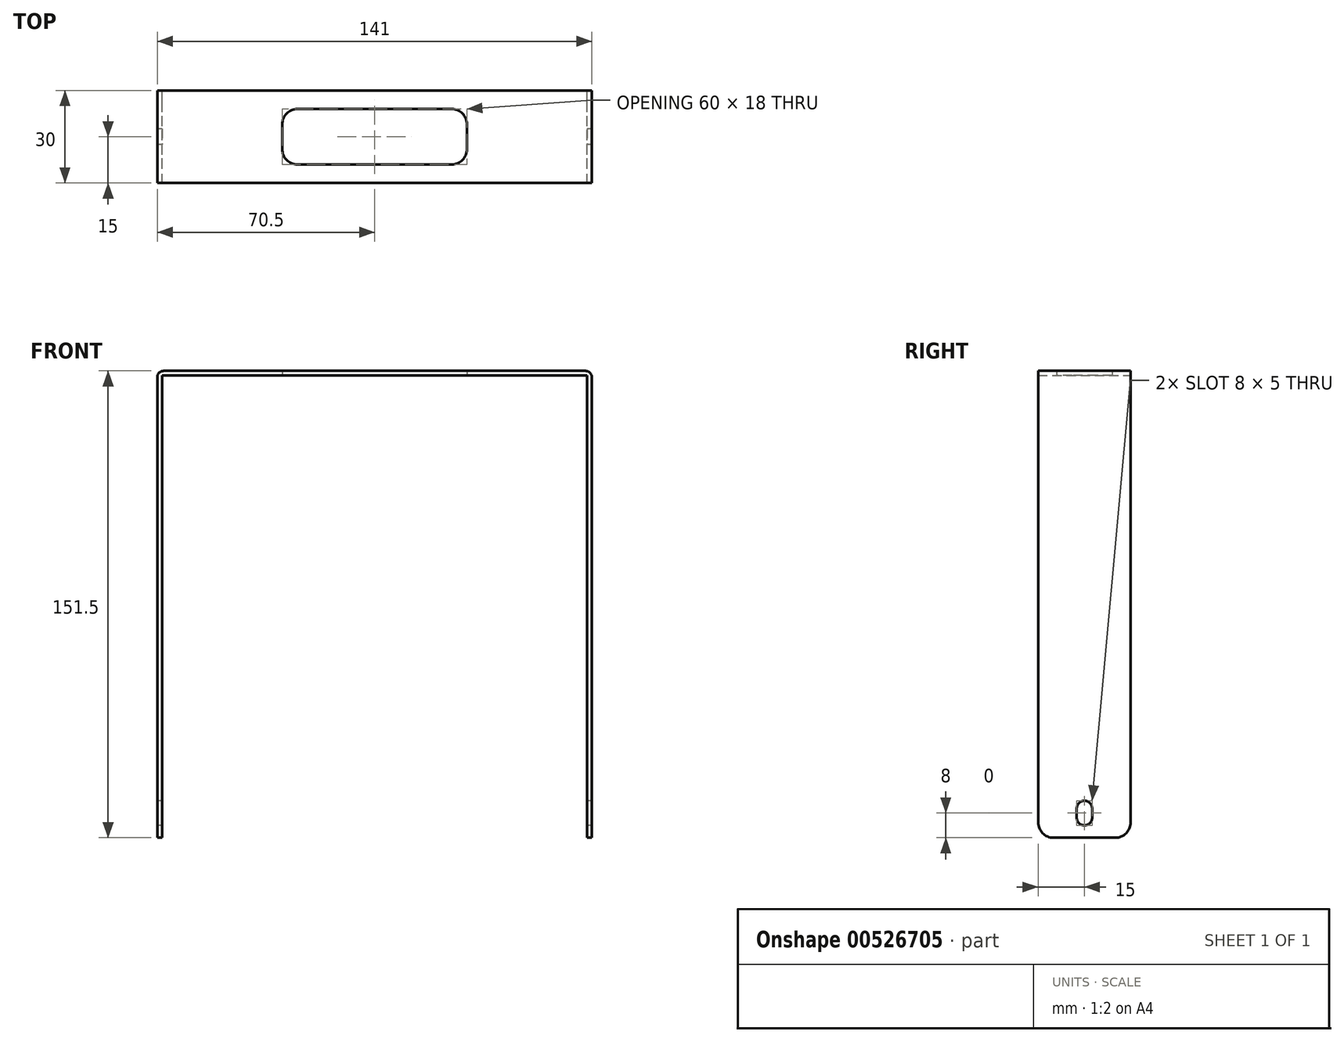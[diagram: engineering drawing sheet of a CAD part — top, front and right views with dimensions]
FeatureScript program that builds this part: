
annotation { "Feature Type Name" : "Feature", "Feature Type Description" : "" }
export const myFeature = defineFeature(function(context is Context, id is Id, definition is map)
    precondition{}
    {
        {
            var Q0;
            Q0=qCreatedBy(makeId("Top.planeOp"),FACE);
            var sketch = newSketch(context, id + "F0", { "sketchPlane" : qUnion([Q0])});
            skLineSegment(sketch, "E0.bottom", {"start": v(-70.5, 15) * mm, "end": v(70.5, 15) * mm});
            skLineSegment(sketch, "E0.top", {"start": v(-70.5, -15) * mm, "end": v(70.5, -15) * mm});
            skLineSegment(sketch, "E0.left", {"start": v(-70.5, 15) * mm, "end": v(-70.5, -15) * mm});
            skLineSegment(sketch, "E0.right", {"start": v(70.5, 15) * mm, "end": v(70.5, -15) * mm});
            skPoint(sketch, "E0.middle", {"position": v(0, 0) * mm});
            skLineSegment(sketch, "E1.bottom", {"start": v(-30, 9) * mm, "end": v(30, 9) * mm});
            skLineSegment(sketch, "E1.top", {"start": v(-30, -9) * mm, "end": v(30, -9) * mm});
            skLineSegment(sketch, "E1.left", {"start": v(-30, 9) * mm, "end": v(-30, -9) * mm});
            skLineSegment(sketch, "E1.right", {"start": v(30, 9) * mm, "end": v(30, -9) * mm});
            skSolve(sketch);
        }
        {
            var Q0;
            Q0=makeQuery(id+"F0.imprint","IMPRINT",FACE,{"disambiguationData":[TD([[makeQuery(id+"F0.imprint","IMPRINT",EDGE,{"derivedFrom":sQuery(id+"F0.wireOp",EDGE,"E0.bottom")}),-1.0]])]});
            extrude(context, id + "F1", {"entities" : qUnion([Q0]), "depth" : 1.5 * mm});
        }
        {
            var Q0;
            Q0=makeQuery(id+"F1.opExtrude","CAP_FACE",FACE,{"disambiguationData":[OSD([sQuery(id+"F0.wireOp",EDGE,"E0.bottom"),sQuery(id+"F0.wireOp",EDGE,"E0.top"),sQuery(id+"F0.wireOp",EDGE,"E0.left"),sQuery(id+"F0.wireOp",EDGE,"E0.right"),sQuery(id+"F0.wireOp",EDGE,"E1.bottom"),sQuery(id+"F0.wireOp",EDGE,"E1.top"),sQuery(id+"F0.wireOp",EDGE,"E1.left"),sQuery(id+"F0.wireOp",EDGE,"E1.right")])],"isStart":true});
            var sketch = newSketch(context, id + "F2", { "sketchPlane" : qUnion([Q0])});
            skLineSegment(sketch, "E2.bottom", {"start": v(-70.5, 15) * mm, "end": v(-69, 15) * mm});
            skLineSegment(sketch, "E2.top", {"start": v(-70.5, -15) * mm, "end": v(-69, -15) * mm});
            skLineSegment(sketch, "E2.left", {"start": v(-70.5, 15) * mm, "end": v(-70.5, -15) * mm});
            skLineSegment(sketch, "E2.right", {"start": v(-69, 15) * mm, "end": v(-69, -15) * mm});
            skLineSegment(sketch, "E3.bottom", {"start": v(70.5, 15) * mm, "end": v(69, 15) * mm});
            skLineSegment(sketch, "E3.top", {"start": v(70.5, -15) * mm, "end": v(69, -15) * mm});
            skLineSegment(sketch, "E3.left", {"start": v(70.5, 15) * mm, "end": v(70.5, -15) * mm});
            skLineSegment(sketch, "E3.right", {"start": v(69, 15) * mm, "end": v(69, -15) * mm});
            skSolve(sketch);
        }
        {
            var Q0;
            Q0=makeQuery(id+"F2.imprint","IMPRINT",FACE,{"disambiguationData":[TD([[makeQuery(id+"F2.imprint","IMPRINT",EDGE,{"derivedFrom":sQuery(id+"F2.wireOp",EDGE,"E2.bottom")}),-1.0]])]});
            var Q1;
            Q1=makeQuery(id+"F2.imprint","IMPRINT",FACE,{"disambiguationData":[TD([[makeQuery(id+"F2.imprint","IMPRINT",EDGE,{"derivedFrom":sQuery(id+"F2.wireOp",EDGE,"E3.bottom")}),-1.0]])]});
            extrude(context, id + "F3", {"entities" : qUnion([Q0, Q1]), "operationType" : NewBodyOperationType.ADD, "depth" : 150 * mm, "offsetDistance" : 25 * mm});
        }
        {
            var Q0;
            Q0=makeQuery(id+"F0S0k0WWYooROMG_1.opExtrude","SWEPT_EDGE",EDGE,{"disambiguationData":[OSD([sQuery(id+"FLBt2EZMuTxA5II_1.wireOp",EDGE,"gpiNC70y-X5YM-kdtF-PmHe-AwHMzD0TUCJG.top"),sQuery(id+"FLBt2EZMuTxA5II_1.wireOp",EDGE,"gpiNC70y-X5YM-kdtF-PmHe-AwHMzD0TUCJG.right")])]});
            var Q1;
            Q1=makeQuery(id+"F0S0k0WWYooROMG_1.opExtrude","SWEPT_EDGE",EDGE,{"disambiguationData":[OSD([sQuery(id+"FLBt2EZMuTxA5II_1.wireOp",EDGE,"gpiNC70y-X5YM-kdtF-PmHe-AwHMzD0TUCJG.bottom"),sQuery(id+"FLBt2EZMuTxA5II_1.wireOp",EDGE,"gpiNC70y-X5YM-kdtF-PmHe-AwHMzD0TUCJG.right")])]});
            var Q2;
            Q2=makeQuery(id+"FBcZxHqoujWJ6ID_1.1.F0S0k0WWYooROMG_1.opExtrude","SWEPT_EDGE",EDGE,{"disambiguationData":[OSD([sQuery(id+"FLBt2EZMuTxA5II_1.wireOp",EDGE,"gpiNC70y-X5YM-kdtF-PmHe-AwHMzD0TUCJG.top"),sQuery(id+"FLBt2EZMuTxA5II_1.wireOp",EDGE,"gpiNC70y-X5YM-kdtF-PmHe-AwHMzD0TUCJG.right")])]});
            var Q3;
            Q3=makeQuery(id+"FBcZxHqoujWJ6ID_1.1.F0S0k0WWYooROMG_1.opExtrude","SWEPT_EDGE",EDGE,{"disambiguationData":[OSD([sQuery(id+"FLBt2EZMuTxA5II_1.wireOp",EDGE,"gpiNC70y-X5YM-kdtF-PmHe-AwHMzD0TUCJG.bottom"),sQuery(id+"FLBt2EZMuTxA5II_1.wireOp",EDGE,"gpiNC70y-X5YM-kdtF-PmHe-AwHMzD0TUCJG.right")])]});
            var Q4;
            Q4=makeQuery(id+"F1.opExtrude","SWEPT_EDGE",EDGE,{"disambiguationData":[OSD([sQuery(id+"F0.wireOp",EDGE,"E1.bottom"),sQuery(id+"F0.wireOp",EDGE,"E1.right")])]});
            var Q5;
            Q5=makeQuery(id+"F1.opExtrude","SWEPT_EDGE",EDGE,{"disambiguationData":[OSD([sQuery(id+"F0.wireOp",EDGE,"E1.top"),sQuery(id+"F0.wireOp",EDGE,"E1.right")])]});
            var Q6;
            Q6=makeQuery(id+"F1.opExtrude","SWEPT_EDGE",EDGE,{"disambiguationData":[OSD([sQuery(id+"F0.wireOp",EDGE,"E1.top"),sQuery(id+"F0.wireOp",EDGE,"E1.left")])]});
            var Q7;
            Q7=makeQuery(id+"F1.opExtrude","SWEPT_EDGE",EDGE,{"disambiguationData":[OSD([sQuery(id+"F0.wireOp",EDGE,"E1.bottom"),sQuery(id+"F0.wireOp",EDGE,"E1.left")])]});
            fillet(context, id + "F4", {"entities" : qUnion([Q0, Q1, Q2, Q3, Q4, Q5, Q6, Q7]), "radius" : 5 * mm, "tangentPropagation" : true, "allowEdgeOverflow" : false});
        }
        {
            var Q0;
            Q0=makeQuery(id+"F3.opExtrude","CAP_EDGE",EDGE,{"disambiguationData":[OSD([sQuery(id+"F2.wireOp",EDGE,"E2.bottom")])],"isStart":false});
            var Q1;
            Q1=makeQuery(id+"F3.opExtrude","CAP_EDGE",EDGE,{"disambiguationData":[OSD([sQuery(id+"F2.wireOp",EDGE,"E2.top")])],"isStart":false});
            var Q2;
            Q2=makeQuery(id+"F3.opExtrude","CAP_EDGE",EDGE,{"disambiguationData":[OSD([sQuery(id+"F2.wireOp",EDGE,"E3.bottom")])],"isStart":false});
            var Q3;
            Q3=makeQuery(id+"F3.opExtrude","CAP_EDGE",EDGE,{"disambiguationData":[OSD([sQuery(id+"F2.wireOp",EDGE,"E3.top")])],"isStart":false});
            fillet(context, id + "F5", {"entities" : qUnion([Q0, Q1, Q2, Q3]), "radius" : 5 * mm, "tangentPropagation" : true, "allowEdgeOverflow" : false});
        }
        {
            var Q0;
            Q0=makeQuery(id+"F3.boolean.opBoolean","MERGE",FACE,{"derivedFrom":[makeQuery(id+"F1.opExtrude","SWEPT_FACE",FACE,{"disambiguationData":[OSD([sQuery(id+"F0.wireOp",EDGE,"E0.left")])]}),makeQuery(id+"F3.opExtrude","SWEPT_FACE",FACE,{"disambiguationData":[OSD([sQuery(id+"F2.wireOp",EDGE,"E2.left")])]})]});
            var sketch = newSketch(context, id + "F6", { "sketchPlane" : qUnion([Q0])});
            skLineSegment(sketch, "E4", {"start": v(0, -150) * mm, "end": v(0, 1.5) * mm, "construction": true});
            skLineSegment(sketch, "E5.bottom", {"start": v(0, -146) * mm, "end": v(0, -146) * mm});
            skLineSegment(sketch, "E5.top", {"start": v(0, -138) * mm, "end": v(0, -138) * mm});
            skLineSegment(sketch, "E5.left", {"start": v(-2.5, -143.5) * mm, "end": v(-2.5, -140.5) * mm});
            skLineSegment(sketch, "E5.right", {"start": v(2.5, -143.5) * mm, "end": v(2.5, -140.5) * mm});
            skPoint(sketch, "E5.middle", {"position": v(0, -142) * mm});
            skPoint(sketch, "E6.visualSharp", {"position": v(-2.5, -138) * mm});
            skArc(sketch, "E6.filletArc", {"start": v(0, -138) * mm, "mid": v(-1.77, -138.73) * mm, "end": v(-2.5, -140.5) * mm});
            skPoint(sketch, "E7.visualSharp", {"position": v(2.5, -138) * mm});
            skArc(sketch, "E7.filletArc", {"start": v(2.5, -140.5) * mm, "mid": v(1.77, -138.73) * mm, "end": v(0, -138) * mm});
            skPoint(sketch, "E8.visualSharp", {"position": v(-2.5, -146) * mm});
            skArc(sketch, "E8.filletArc", {"start": v(-2.5, -143.5) * mm, "mid": v(-1.77, -145.27) * mm, "end": v(0, -146) * mm});
            skPoint(sketch, "E9.visualSharp", {"position": v(2.5, -146) * mm});
            skArc(sketch, "E9.filletArc", {"start": v(0, -146) * mm, "mid": v(1.77, -145.27) * mm, "end": v(2.5, -143.5) * mm});
            skSolve(sketch);
        }
        {
            var Q0;
            Q0=makeQuery(id+"F6.imprint","IMPRINT",FACE,{"disambiguationData":[TD([[makeQuery(id+"F6.imprint","IMPRINT",EDGE,{"derivedFrom":sQuery(id+"F6.wireOp",EDGE,"E5.left")}),-1.0]])]});
            extrude(context, id + "F7", {"entities" : qUnion([Q0]), "operationType" : NewBodyOperationType.REMOVE, "oppositeDirection" : true, "depth" : 200 * mm, "offsetDistance" : 25 * mm});
        }
        {
            var Q0;
            Q0=makeQuery(id+"F1.opExtrude","CAP_EDGE",EDGE,{"disambiguationData":[OSD([sQuery(id+"F0.wireOp",EDGE,"E0.right")])],"isStart":false});
            var Q1;
            Q1=makeQuery(id+"F1.opExtrude","CAP_EDGE",EDGE,{"disambiguationData":[OSD([sQuery(id+"F0.wireOp",EDGE,"E0.left")])],"isStart":false});
            var Q2;
            Q2=makeQuery(id+"F3.opExtrude","CAP_EDGE",EDGE,{"disambiguationData":[OSD([sQuery(id+"F2.wireOp",EDGE,"E2.right")])],"isStart":true});
            var Q3;
            Q3=makeQuery(id+"F3.opExtrude","CAP_EDGE",EDGE,{"disambiguationData":[OSD([sQuery(id+"F2.wireOp",EDGE,"E3.right")])],"isStart":true});
            fillet(context, id + "F8", {"entities" : qUnion([Q0, Q1, Q2, Q3]), "radius" : 2 * mm, "tangentPropagation" : true, "allowEdgeOverflow" : false});
        }
    });
